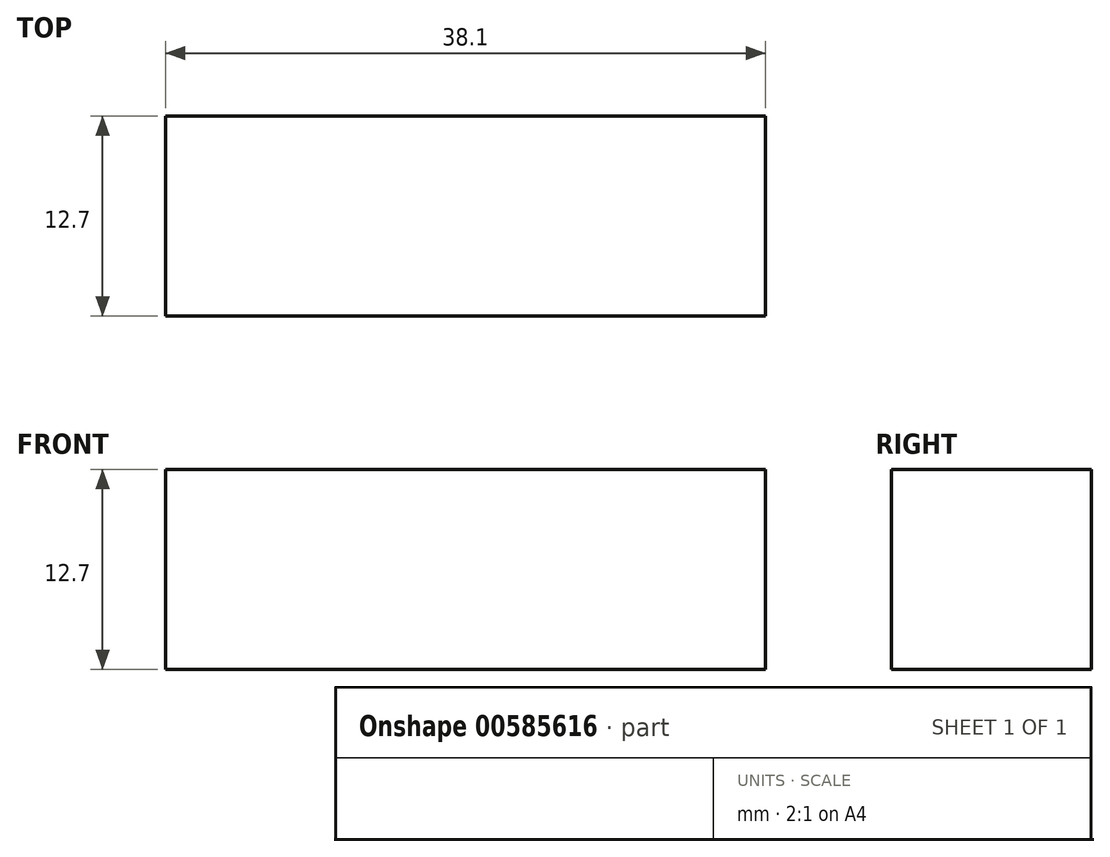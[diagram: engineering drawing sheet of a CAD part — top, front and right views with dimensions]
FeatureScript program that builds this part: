
annotation { "Feature Type Name" : "Feature", "Feature Type Description" : "" }
export const myFeature = defineFeature(function(context is Context, id is Id, definition is map)
    precondition{}
    {
        {
            var Q0;
            Q0=qCreatedBy(makeId("Top.planeOp"),FACE);
            var sketch = newSketch(context, id + "F0", { "sketchPlane" : qUnion([Q0])});
            skLineSegment(sketch, "E0.bottom", {"start": v(-19.05, 6.35) * mm, "end": v(19.05, 6.35) * mm});
            skLineSegment(sketch, "E0.top", {"start": v(-19.05, -6.35) * mm, "end": v(19.05, -6.35) * mm});
            skLineSegment(sketch, "E0.left", {"start": v(-19.05, 6.35) * mm, "end": v(-19.05, -6.35) * mm});
            skLineSegment(sketch, "E0.right", {"start": v(19.05, 6.35) * mm, "end": v(19.05, -6.35) * mm});
            skPoint(sketch, "E0.middle", {"position": v(0, 0) * mm});
            skSolve(sketch);
        }
        {
            var Q0;
            Q0=makeQuery(id+"F0.imprint","IMPRINT",FACE,{"disambiguationData":[TD([[makeQuery(id+"F0.imprint","IMPRINT",EDGE,{"derivedFrom":sQuery(id+"F0.wireOp",EDGE,"E0.bottom")}),-1.0]])]});
            extrude(context, id + "F1", {"entities" : qUnion([Q0]), "depth" : 12.7 * mm, "offsetDistance" : 25.4 * mm});
        }
    });
